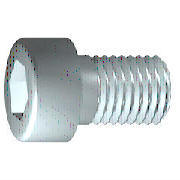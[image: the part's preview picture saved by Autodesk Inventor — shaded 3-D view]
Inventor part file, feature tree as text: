
AUTODESK INVENTOR PART (.ipt)
format: ipt  version: 2018 (Build 220112000, 112)  size: 190,464 bytes
history: native  units: mm (DEFAULTED — no unit token found)
features: sketch x2, extrude x1, plane x1, fillet x1
ambient origin geometry x7: Origin, YZ Plane, XY Plane, X Axis, Y Axis, Z Axis, Center Point
bodies: Solid1 (feature_tree), Body (feature_tree)
feature tree (5):
  extrude  "Slot"  Depth=3.0mm
  plane  "Work Plane1"
  fillet  "Fillet2"  Radius=3.0mm
  sketch  "Sketch1"  dims[d1=8.693275mm d2=0.306825mm d3=3.0mm]
  sketch  "Sketch2"  dims[d4=1.5mm d5=60.0deg d6=3.0mm d7=3.0mm d8=2.886751mm d9=5.5mm d10=90.0deg d11=10.0mm d12=0.0mm d13=8.693275mm d14=0.0mm d15=0.306725mm d16=0.306725mm d17=0.3mm d19=0.0mm d26=10.0mm d27=45.0deg d28=0.0mm d29=0.0mm d30=0.1mm]
